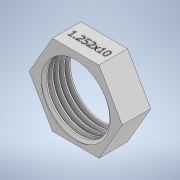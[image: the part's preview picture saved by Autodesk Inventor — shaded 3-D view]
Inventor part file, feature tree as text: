
AUTODESK INVENTOR PART (.ipt)
format: ipt  version: 2021.1 (Build 251245010, 245A)  size: 560,640 bytes
history: native  units: in
note: dims shown in document units (in); Inventor stores cm internally (conversion verified against a paired STEP export)
features: sketch x5, extrude x4, helix x1
ambient origin geometry x8: Origin, YZ Plane, XZ Plane, XY Plane, X Axis, Y Axis, Z Axis, Center Point
bodies: Solid1 (feature_tree)
feature tree (10):
  extrude  "Extrusion1"  Depth=0.125in
  helix  "Coil1"  [1 undecoded]
  extrude  "Extrusion2"  TaperAngle=60.0deg  [1 undecoded]
  extrude  "Extrusion3"  Depth=0.0072in
  extrude  "Extrusion4"  TaperAngle=120.0deg  [1 undecoded]
  sketch  "Sketch1"  dims[d0=1.1647in d1=0.125in d2=0.5in d3=0.0in]
  sketch  "Sketch2"  dims[d4=0.0072in d5=60.0deg]
  sketch  "Sketch3"  dims[d7=120.0deg d8=0.0072in]
  sketch  "Sketch4"  dims[d9=60.0deg d10=120.0deg]
  sketch  "Sketch5"  dims[d11=0.1in d12=0.05in d13=0.5824in d15=0.1in d16=0.7in d17=0.3937in d18=0.0in d19=90.0deg d20=90.0deg d21=0.0in d22=0.0in d23=0.5in d24=0.0in d25=0.6394in d26=0.05in d27=0.0in d28=0.05in d29=0.0in]
note: 3 required parameter values undecoded (feature->parameter linkage not recoverable at this tier; creation-order binding heuristic only, values carry confidence <= 0.55)
